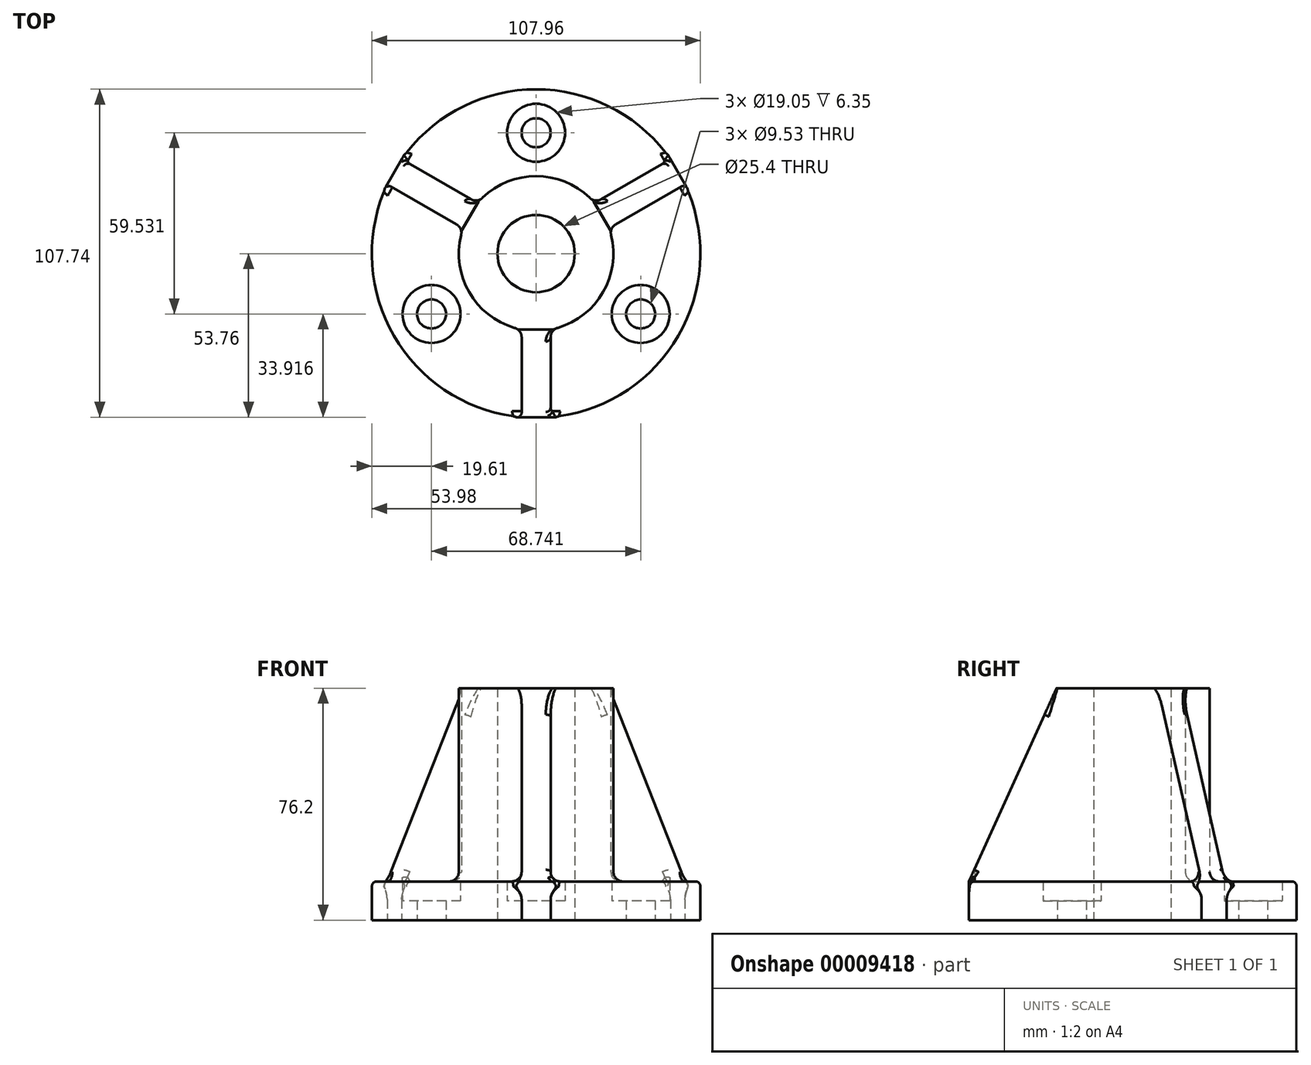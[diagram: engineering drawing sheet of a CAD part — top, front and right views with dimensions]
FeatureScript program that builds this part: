
annotation { "Feature Type Name" : "Feature", "Feature Type Description" : "" }
export const myFeature = defineFeature(function(context is Context, id is Id, definition is map)
    precondition{}
    {
        {
            var Q0;
            Q0=qCreatedBy(makeId("Top.planeOp"),FACE);
            var sketch = newSketch(context, id + "F0", { "sketchPlane" : qUnion([Q0])});
            skArc(sketch, "E0", {"start": v(-48.94, 22.76) * mm, "mid": v(-46.74, -26.99) * mm, "end": v(-4.76, -53.76) * mm});
            skArc(sketch, "E1", {"start": v(-23.99, 8.35) * mm, "mid": v(-22, -12.7) * mm, "end": v(-4.76, -24.95) * mm});
            skCircle(sketch, "E2", {"center": v(0, 0) * mm, "radius": 12.7 * mm});
            skCircle(sketch, "E3", {"center": v(0, 39.69) * mm, "radius": 4.76 * mm});
            skCircle(sketch, "E4", {"center": v(0, 39.69) * mm, "radius": 9.53 * mm});
            skCircle(sketch, "E5.1.0", {"center": v(-34.37, -19.84) * mm, "radius": 4.76 * mm});
            skCircle(sketch, "E5.1.1", {"center": v(-34.37, -19.84) * mm, "radius": 9.53 * mm});
            skCircle(sketch, "E5.2.0", {"center": v(34.37, -19.84) * mm, "radius": 4.76 * mm});
            skCircle(sketch, "E5.2.1", {"center": v(34.37, -19.84) * mm, "radius": 9.53 * mm});
            skLineSegment(sketch, "E6", {"start": v(0, 0) * mm, "end": v(-73.96, 42.7) * mm, "construction": true});
            skLineSegment(sketch, "E7", {"start": v(-23.99, 8.35) * mm, "end": v(-19.23, 16.6) * mm});
            skLineSegment(sketch, "E8", {"start": v(-19.23, 16.6) * mm, "end": v(-44.18, 31) * mm});
            skLineSegment(sketch, "E9", {"start": v(-23.99, 8.35) * mm, "end": v(-48.94, 22.76) * mm});
            skLineSegment(sketch, "E10.1.0", {"start": v(-4.76, -24.95) * mm, "end": v(-4.76, -53.76) * mm});
            skLineSegment(sketch, "E10.1.1", {"start": v(4.76, -24.95) * mm, "end": v(4.76, -53.76) * mm});
            skLineSegment(sketch, "E10.1.2", {"start": v(4.76, -24.95) * mm, "end": v(-4.76, -24.95) * mm});
            skLineSegment(sketch, "E10.2.0", {"start": v(23.99, 8.35) * mm, "end": v(48.94, 22.76) * mm});
            skLineSegment(sketch, "E10.2.1", {"start": v(19.23, 16.6) * mm, "end": v(44.18, 31) * mm});
            skLineSegment(sketch, "E10.2.2", {"start": v(19.23, 16.6) * mm, "end": v(23.99, 8.35) * mm});
            skArc(sketch, "E11.trimOffspring", {"start": v(19.23, 16.6) * mm, "mid": v(0, 25.4) * mm, "end": v(-19.23, 16.6) * mm});
            skArc(sketch, "E12.trimOffspring", {"start": v(4.76, -24.95) * mm, "mid": v(22, -12.7) * mm, "end": v(23.99, 8.35) * mm});
            skArc(sketch, "E13.trimOffspring", {"start": v(4.76, -53.76) * mm, "mid": v(46.74, -26.99) * mm, "end": v(48.94, 22.76) * mm});
            skArc(sketch, "E14.trimOffspring", {"start": v(44.18, 31) * mm, "mid": v(0, 53.98) * mm, "end": v(-44.18, 31) * mm});
            skLineSegment(sketch, "E15", {"start": v(-4.76, -53.76) * mm, "end": v(4.76, -53.76) * mm});
            skLineSegment(sketch, "E16", {"start": v(48.94, 22.76) * mm, "end": v(44.18, 31) * mm});
            skLineSegment(sketch, "E17", {"start": v(-48.94, 22.76) * mm, "end": v(-44.18, 31) * mm});
            skSolve(sketch);
        }
        {
            var Q0;
            Q0=makeQuery(id+"F0.imprint","IMPRINT",FACE,{"disambiguationData":[TD([[makeQuery(id+"F0.imprint","IMPRINT",EDGE,{"derivedFrom":sQuery(id+"F0.wireOp",EDGE,"E1")}),1.0]])]});
            var Q1;
            Q1=makeQuery(id+"F0.imprint","IMPRINT",FACE,{"disambiguationData":[TD([[makeQuery(id+"F0.imprint","IMPRINT",EDGE,{"derivedFrom":sQuery(id+"F0.wireOp",EDGE,"E7")}),1.0]])]});
            var Q2;
            {var subQ1=sQuery(id+"F0.wireOp",EDGE,"E10.2.0");Q2=makeQuery(id+"F0.imprint","IMPRINT",FACE,{"disambiguationData":[TD([[makeQuery(id+"F0.imprint","IMPRINT",EDGE,{"derivedFrom":subQ1}),1.0]])]});}
            var Q3;
            {var subQ1=sQuery(id+"F0.wireOp",EDGE,"E10.1.0");Q3=makeQuery(id+"F0.imprint","IMPRINT",FACE,{"disambiguationData":[TD([[makeQuery(id+"F0.imprint","IMPRINT",EDGE,{"derivedFrom":subQ1}),1.0]])]});}
            extrude(context, id + "F1", {"entities" : qUnion([Q0, Q1, Q2, Q3]), "depth" : 76.2 * mm});
        }
        {
            var Q0;
            Q0=makeQuery(id+"F0.imprint","IMPRINT",FACE,{"disambiguationData":[TD([[makeQuery(id+"F0.imprint","IMPRINT",EDGE,{"derivedFrom":sQuery(id+"F0.wireOp",EDGE,"E4")}),-1.0]])]});
            var Q1;
            {var subQ1=sQuery(id+"F0.wireOp",EDGE,"E10.2.0");Q1=makeQuery(id+"F0.imprint","IMPRINT",FACE,{"disambiguationData":[TD([[makeQuery(id+"F0.imprint","IMPRINT",EDGE,{"derivedFrom":subQ1}),1.0]])]});}
            var Q2;
            Q2=makeQuery(id+"F0.imprint","IMPRINT",FACE,{"disambiguationData":[TD([[makeQuery(id+"F0.imprint","IMPRINT",EDGE,{"derivedFrom":sQuery(id+"F0.wireOp",EDGE,"E5.2.1")}),-1.0]])]});
            var Q3;
            {var subQ1=sQuery(id+"F0.wireOp",EDGE,"E10.1.0");Q3=makeQuery(id+"F0.imprint","IMPRINT",FACE,{"disambiguationData":[TD([[makeQuery(id+"F0.imprint","IMPRINT",EDGE,{"derivedFrom":subQ1}),1.0]])]});}
            var Q4;
            Q4=makeQuery(id+"F0.imprint","IMPRINT",FACE,{"disambiguationData":[TD([[makeQuery(id+"F0.imprint","IMPRINT",EDGE,{"derivedFrom":sQuery(id+"F0.wireOp",EDGE,"E1")}),-1.0]])]});
            var Q5;
            Q5=makeQuery(id+"F0.imprint","IMPRINT",FACE,{"disambiguationData":[TD([[makeQuery(id+"F0.imprint","IMPRINT",EDGE,{"derivedFrom":sQuery(id+"F0.wireOp",EDGE,"E7")}),1.0]])]});
            extrude(context, id + "F2", {"entities" : qUnion([Q0, Q1, Q2, Q3, Q4, Q5]), "operationType" : NewBodyOperationType.ADD, "depth" : 12.7 * mm});
        }
        {
            var Q0;
            Q0=makeQuery(id+"F0.imprint","IMPRINT",FACE,{"disambiguationData":[TD([[makeQuery(id+"F0.imprint","IMPRINT",EDGE,{"derivedFrom":sQuery(id+"F0.wireOp",EDGE,"E5.1.0")}),-1.0]])]});
            var Q1;
            Q1=makeQuery(id+"F0.imprint","IMPRINT",FACE,{"disambiguationData":[TD([[makeQuery(id+"F0.imprint","IMPRINT",EDGE,{"derivedFrom":sQuery(id+"F0.wireOp",EDGE,"E3")}),-1.0]])]});
            var Q2;
            Q2=makeQuery(id+"F0.imprint","IMPRINT",FACE,{"disambiguationData":[TD([[makeQuery(id+"F0.imprint","IMPRINT",EDGE,{"derivedFrom":sQuery(id+"F0.wireOp",EDGE,"E5.2.0")}),-1.0]])]});
            extrude(context, id + "F3", {"entities" : qUnion([Q0, Q1, Q2]), "operationType" : NewBodyOperationType.ADD, "depth" : 6.35 * mm});
        }
        {
            var Q0;
            Q0=makeQuery(id+"F1.opExtrude","SWEPT_FACE",FACE,{"disambiguationData":[OSD([sQuery(id+"F0.wireOp",EDGE,"E9")])]});
            var sketch = newSketch(context, id + "F4", { "sketchPlane" : qUnion([Q0])});
            skLineSegment(sketch, "E18", {"start": v(-24.95, 12.7) * mm, "end": v(-53.76, 12.7) * mm});
            skLineSegment(sketch, "E19", {"start": v(-53.76, 12.7) * mm, "end": v(-24.95, 76.2) * mm});
            skLineSegment(sketch, "E20", {"start": v(-24.95, 76.2) * mm, "end": v(-24.95, 12.7) * mm});
            skSolve(sketch);
        }
        {
            var Q0;
            Q0=makeQuery(id+"F1.opExtrude","SWEPT_FACE",FACE,{"disambiguationData":[OSD([sQuery(id+"F0.wireOp",EDGE,"E10.1.0")])]});
            var sketch = newSketch(context, id + "F5", { "sketchPlane" : qUnion([Q0])});
            skLineSegment(sketch, "E21", {"start": v(53.76, 12.7) * mm, "end": v(24.95, 12.7) * mm});
            skLineSegment(sketch, "E22", {"start": v(24.95, 12.7) * mm, "end": v(24.95, 76.2) * mm});
            skLineSegment(sketch, "E23", {"start": v(24.95, 76.2) * mm, "end": v(53.76, 12.7) * mm});
            skSolve(sketch);
        }
        {
            var Q0;
            Q0=makeQuery(id+"F1.opExtrude","SWEPT_FACE",FACE,{"disambiguationData":[OSD([sQuery(id+"F0.wireOp",EDGE,"E10.2.0")])]});
            var sketch = newSketch(context, id + "F6", { "sketchPlane" : qUnion([Q0])});
            skLineSegment(sketch, "E24", {"start": v(24.95, 76.2) * mm, "end": v(53.76, 12.7) * mm});
            skLineSegment(sketch, "E25", {"start": v(53.76, 12.7) * mm, "end": v(24.95, 12.7) * mm});
            skLineSegment(sketch, "E26", {"start": v(24.95, 12.7) * mm, "end": v(24.95, 76.2) * mm});
            skSolve(sketch);
        }
        {
            var Q0;
            Q0=makeQuery(id+"F6.imprint","IMPRINT",FACE,{"disambiguationData":[TD([[makeQuery(id+"F6.imprint","IMPRINT",EDGE,{"derivedFrom":sQuery(id+"F6.wireOp",EDGE,"E24")}),1.0]])]});
            extrude(context, id + "F7", {"entities" : qUnion([Q0]), "operationType" : NewBodyOperationType.REMOVE, "oppositeDirection" : true, "depth" : 25.4 * mm});
        }
        {
            var Q0;
            Q0=makeQuery(id+"F5.imprint","IMPRINT",FACE,{"disambiguationData":[TD([[makeQuery(id+"F5.imprint","IMPRINT",EDGE,{"derivedFrom":sQuery(id+"F5.wireOp",EDGE,"E23")}),1.0]])]});
            extrude(context, id + "F8", {"entities" : qUnion([Q0]), "operationType" : NewBodyOperationType.REMOVE, "oppositeDirection" : true, "depth" : 25.4 * mm});
        }
        {
            var Q0;
            Q0=makeQuery(id+"F4.imprint","IMPRINT",FACE,{"disambiguationData":[TD([[makeQuery(id+"F4.imprint","IMPRINT",EDGE,{"derivedFrom":sQuery(id+"F4.wireOp",EDGE,"E19")}),1.0]])]});
            extrude(context, id + "F9", {"entities" : qUnion([Q0]), "operationType" : NewBodyOperationType.REMOVE, "oppositeDirection" : true, "depth" : 25.4 * mm});
        }
        {
            var Q0;
            Q0=makeQuery(id+"F2.opExtrude","CAP_EDGE",EDGE,{"disambiguationData":[OSD([sQuery(id+"F0.wireOp",EDGE,"E14.trimOffspring")])],"isStart":false});
            var Q1;
            Q1=makeQuery(id+"F2.opExtrude","CAP_EDGE",EDGE,{"disambiguationData":[OSD([sQuery(id+"F0.wireOp",EDGE,"E13.trimOffspring")])],"isStart":false});
            var Q2;
            Q2=makeQuery(id+"F2.opExtrude","CAP_EDGE",EDGE,{"disambiguationData":[OSD([sQuery(id+"F0.wireOp",EDGE,"E0")])],"isStart":false});
            fillet(context, id + "F10", {"entities" : qUnion([Q0, Q1, Q2]), "radius" : 1.59 * mm, "tangentPropagation" : true, "allowEdgeOverflow" : false});
        }
        {
            var Q0;
            Q0=makeQuery(id+"F1.opExtrude","SWEPT_EDGE",EDGE,{"disambiguationData":[OSD([sQuery(id+"F0.wireOp",EDGE,"E1"),sQuery(id+"F0.wireOp",EDGE,"E7"),sQuery(id+"F0.wireOp",EDGE,"E9")])]});
            var Q1;
            Q1=makeQuery(id+"F1.opExtrude","SWEPT_EDGE",EDGE,{"disambiguationData":[OSD([sQuery(id+"F0.wireOp",EDGE,"E1"),sQuery(id+"F0.wireOp",EDGE,"E10.1.0"),sQuery(id+"F0.wireOp",EDGE,"E10.1.2")])]});
            var Q2;
            Q2=makeQuery(id+"F1.opExtrude","SWEPT_EDGE",EDGE,{"disambiguationData":[OSD([sQuery(id+"F0.wireOp",EDGE,"E10.1.1"),sQuery(id+"F0.wireOp",EDGE,"E10.1.2"),sQuery(id+"F0.wireOp",EDGE,"E12.trimOffspring")])]});
            var Q3;
            Q3=makeQuery(id+"F1.opExtrude","SWEPT_EDGE",EDGE,{"disambiguationData":[OSD([sQuery(id+"F0.wireOp",EDGE,"E10.2.0"),sQuery(id+"F0.wireOp",EDGE,"E10.2.2"),sQuery(id+"F0.wireOp",EDGE,"E12.trimOffspring")])]});
            var Q4;
            Q4=makeQuery(id+"F1.opExtrude","SWEPT_EDGE",EDGE,{"disambiguationData":[OSD([sQuery(id+"F0.wireOp",EDGE,"E10.2.1"),sQuery(id+"F0.wireOp",EDGE,"E10.2.2"),sQuery(id+"F0.wireOp",EDGE,"E11.trimOffspring")])]});
            var Q5;
            Q5=makeQuery(id+"F1.opExtrude","SWEPT_EDGE",EDGE,{"disambiguationData":[OSD([sQuery(id+"F0.wireOp",EDGE,"E7"),sQuery(id+"F0.wireOp",EDGE,"E8"),sQuery(id+"F0.wireOp",EDGE,"E11.trimOffspring")])]});
            var Q6;
            Q6=makeQuery(id+"F2.opExtrude","CAP_EDGE",EDGE,{"disambiguationData":[OSD([sQuery(id+"F0.wireOp",EDGE,"E11.trimOffspring")])],"isStart":false});
            var Q7;
            Q7=makeQuery(id+"F2.opExtrude","CAP_EDGE",EDGE,{"disambiguationData":[OSD([sQuery(id+"F0.wireOp",EDGE,"E12.trimOffspring")])],"isStart":false});
            var Q8;
            Q8=makeQuery(id+"F2.opExtrude","CAP_EDGE",EDGE,{"disambiguationData":[OSD([sQuery(id+"F0.wireOp",EDGE,"E1")])],"isStart":false});
            fillet(context, id + "F11", {"entities" : qUnion([Q0, Q1, Q2, Q3, Q4, Q5, Q6, Q7, Q8]), "radius" : 3.17 * mm, "allowEdgeOverflow" : false});
        }
        {
            var Q0;
            Q0=makeQuery(id+"F2.boolean.opBoolean","INTERSECT",EDGE,{"derivedFrom":[makeQuery(id+"F1.opExtrude","SWEPT_FACE",FACE,{"disambiguationData":[OSD([sQuery(id+"F0.wireOp",EDGE,"E10.1.1")])]}),makeQuery(id+"F2.opExtrude","CAP_FACE",FACE,{"disambiguationData":[OSD([sQuery(id+"F0.wireOp",EDGE,"E0"),sQuery(id+"F0.wireOp",EDGE,"E1"),sQuery(id+"F0.wireOp",EDGE,"E4"),sQuery(id+"F0.wireOp",EDGE,"E5.1.1"),sQuery(id+"F0.wireOp",EDGE,"E5.2.1"),sQuery(id+"F0.wireOp",EDGE,"E7"),sQuery(id+"F0.wireOp",EDGE,"E10.1.2"),sQuery(id+"F0.wireOp",EDGE,"E10.2.2"),sQuery(id+"F0.wireOp",EDGE,"E11.trimOffspring"),sQuery(id+"F0.wireOp",EDGE,"E12.trimOffspring"),sQuery(id+"F0.wireOp",EDGE,"E13.trimOffspring"),sQuery(id+"F0.wireOp",EDGE,"E14.trimOffspring"),sQuery(id+"F0.wireOp",EDGE,"E15"),sQuery(id+"F0.wireOp",EDGE,"E16"),sQuery(id+"F0.wireOp",EDGE,"E17")])],"isStart":false})]});
            var Q1;
            Q1=makeQuery(id+"F2.boolean.opBoolean","INTERSECT",EDGE,{"derivedFrom":[makeQuery(id+"F1.opExtrude","SWEPT_FACE",FACE,{"disambiguationData":[OSD([sQuery(id+"F0.wireOp",EDGE,"E10.2.0")])]}),makeQuery(id+"F2.opExtrude","CAP_FACE",FACE,{"disambiguationData":[OSD([sQuery(id+"F0.wireOp",EDGE,"E0"),sQuery(id+"F0.wireOp",EDGE,"E1"),sQuery(id+"F0.wireOp",EDGE,"E4"),sQuery(id+"F0.wireOp",EDGE,"E5.1.1"),sQuery(id+"F0.wireOp",EDGE,"E5.2.1"),sQuery(id+"F0.wireOp",EDGE,"E7"),sQuery(id+"F0.wireOp",EDGE,"E10.1.2"),sQuery(id+"F0.wireOp",EDGE,"E10.2.2"),sQuery(id+"F0.wireOp",EDGE,"E11.trimOffspring"),sQuery(id+"F0.wireOp",EDGE,"E12.trimOffspring"),sQuery(id+"F0.wireOp",EDGE,"E13.trimOffspring"),sQuery(id+"F0.wireOp",EDGE,"E14.trimOffspring"),sQuery(id+"F0.wireOp",EDGE,"E15"),sQuery(id+"F0.wireOp",EDGE,"E16"),sQuery(id+"F0.wireOp",EDGE,"E17")])],"isStart":false})]});
            var Q2;
            Q2=makeQuery(id+"F2.boolean.opBoolean","INTERSECT",EDGE,{"derivedFrom":[makeQuery(id+"F1.opExtrude","SWEPT_FACE",FACE,{"disambiguationData":[OSD([sQuery(id+"F0.wireOp",EDGE,"E10.2.1")])]}),makeQuery(id+"F2.opExtrude","CAP_FACE",FACE,{"disambiguationData":[OSD([sQuery(id+"F0.wireOp",EDGE,"E0"),sQuery(id+"F0.wireOp",EDGE,"E1"),sQuery(id+"F0.wireOp",EDGE,"E4"),sQuery(id+"F0.wireOp",EDGE,"E5.1.1"),sQuery(id+"F0.wireOp",EDGE,"E5.2.1"),sQuery(id+"F0.wireOp",EDGE,"E7"),sQuery(id+"F0.wireOp",EDGE,"E10.1.2"),sQuery(id+"F0.wireOp",EDGE,"E10.2.2"),sQuery(id+"F0.wireOp",EDGE,"E11.trimOffspring"),sQuery(id+"F0.wireOp",EDGE,"E12.trimOffspring"),sQuery(id+"F0.wireOp",EDGE,"E13.trimOffspring"),sQuery(id+"F0.wireOp",EDGE,"E14.trimOffspring"),sQuery(id+"F0.wireOp",EDGE,"E15"),sQuery(id+"F0.wireOp",EDGE,"E16"),sQuery(id+"F0.wireOp",EDGE,"E17")])],"isStart":false})]});
            var Q3;
            Q3=makeQuery(id+"F2.boolean.opBoolean","INTERSECT",EDGE,{"derivedFrom":[makeQuery(id+"F1.opExtrude","SWEPT_FACE",FACE,{"disambiguationData":[OSD([sQuery(id+"F0.wireOp",EDGE,"E8")])]}),makeQuery(id+"F2.opExtrude","CAP_FACE",FACE,{"disambiguationData":[OSD([sQuery(id+"F0.wireOp",EDGE,"E0"),sQuery(id+"F0.wireOp",EDGE,"E1"),sQuery(id+"F0.wireOp",EDGE,"E4"),sQuery(id+"F0.wireOp",EDGE,"E5.1.1"),sQuery(id+"F0.wireOp",EDGE,"E5.2.1"),sQuery(id+"F0.wireOp",EDGE,"E7"),sQuery(id+"F0.wireOp",EDGE,"E10.1.2"),sQuery(id+"F0.wireOp",EDGE,"E10.2.2"),sQuery(id+"F0.wireOp",EDGE,"E11.trimOffspring"),sQuery(id+"F0.wireOp",EDGE,"E12.trimOffspring"),sQuery(id+"F0.wireOp",EDGE,"E13.trimOffspring"),sQuery(id+"F0.wireOp",EDGE,"E14.trimOffspring"),sQuery(id+"F0.wireOp",EDGE,"E15"),sQuery(id+"F0.wireOp",EDGE,"E16"),sQuery(id+"F0.wireOp",EDGE,"E17")])],"isStart":false})]});
            var Q4;
            Q4=makeQuery(id+"F2.boolean.opBoolean","INTERSECT",EDGE,{"derivedFrom":[makeQuery(id+"F1.opExtrude","SWEPT_FACE",FACE,{"disambiguationData":[OSD([sQuery(id+"F0.wireOp",EDGE,"E9")])]}),makeQuery(id+"F2.opExtrude","CAP_FACE",FACE,{"disambiguationData":[OSD([sQuery(id+"F0.wireOp",EDGE,"E0"),sQuery(id+"F0.wireOp",EDGE,"E1"),sQuery(id+"F0.wireOp",EDGE,"E4"),sQuery(id+"F0.wireOp",EDGE,"E5.1.1"),sQuery(id+"F0.wireOp",EDGE,"E5.2.1"),sQuery(id+"F0.wireOp",EDGE,"E7"),sQuery(id+"F0.wireOp",EDGE,"E10.1.2"),sQuery(id+"F0.wireOp",EDGE,"E10.2.2"),sQuery(id+"F0.wireOp",EDGE,"E11.trimOffspring"),sQuery(id+"F0.wireOp",EDGE,"E12.trimOffspring"),sQuery(id+"F0.wireOp",EDGE,"E13.trimOffspring"),sQuery(id+"F0.wireOp",EDGE,"E14.trimOffspring"),sQuery(id+"F0.wireOp",EDGE,"E15"),sQuery(id+"F0.wireOp",EDGE,"E16"),sQuery(id+"F0.wireOp",EDGE,"E17")])],"isStart":false})]});
            var Q5;
            Q5=makeQuery(id+"F2.boolean.opBoolean","INTERSECT",EDGE,{"derivedFrom":[makeQuery(id+"F1.opExtrude","SWEPT_FACE",FACE,{"disambiguationData":[OSD([sQuery(id+"F0.wireOp",EDGE,"E10.1.0")])]}),makeQuery(id+"F2.opExtrude","CAP_FACE",FACE,{"disambiguationData":[OSD([sQuery(id+"F0.wireOp",EDGE,"E0"),sQuery(id+"F0.wireOp",EDGE,"E1"),sQuery(id+"F0.wireOp",EDGE,"E4"),sQuery(id+"F0.wireOp",EDGE,"E5.1.1"),sQuery(id+"F0.wireOp",EDGE,"E5.2.1"),sQuery(id+"F0.wireOp",EDGE,"E7"),sQuery(id+"F0.wireOp",EDGE,"E10.1.2"),sQuery(id+"F0.wireOp",EDGE,"E10.2.2"),sQuery(id+"F0.wireOp",EDGE,"E11.trimOffspring"),sQuery(id+"F0.wireOp",EDGE,"E12.trimOffspring"),sQuery(id+"F0.wireOp",EDGE,"E13.trimOffspring"),sQuery(id+"F0.wireOp",EDGE,"E14.trimOffspring"),sQuery(id+"F0.wireOp",EDGE,"E15"),sQuery(id+"F0.wireOp",EDGE,"E16"),sQuery(id+"F0.wireOp",EDGE,"E17")])],"isStart":false})]});
            fillet(context, id + "F12", {"entities" : qUnion([Q0, Q1, Q2, Q3, Q4, Q5]), "radius" : 3.17 * mm, "tangentPropagation" : true, "allowEdgeOverflow" : false});
        }
        {
            var Q0;
            Q0=makeQuery(id+"F7.boolean.opBoolean","COPY",EDGE,{"derivedFrom":makeQuery(id+"F7.opExtrude","CAP_EDGE",EDGE,{"disambiguationData":[OSD([sQuery(id+"F6.wireOp",EDGE,"E24")])],"isStart":true})});
            var Q1;
            Q1=makeQuery(id+"F7.boolean.opBoolean","INTERSECT",EDGE,{"derivedFrom":[makeQuery(id+"F1.opExtrude","SWEPT_FACE",FACE,{"disambiguationData":[OSD([sQuery(id+"F0.wireOp",EDGE,"E10.2.1")])]}),makeQuery(id+"F7.opExtrude","SWEPT_FACE",FACE,{"disambiguationData":[OSD([sQuery(id+"F6.wireOp",EDGE,"E24")])]})]});
            var Q2;
            Q2=makeQuery(id+"F8.boolean.opBoolean","COPY",EDGE,{"derivedFrom":makeQuery(id+"F8.opExtrude","CAP_EDGE",EDGE,{"disambiguationData":[OSD([sQuery(id+"F5.wireOp",EDGE,"E23")])],"isStart":true})});
            var Q3;
            Q3=makeQuery(id+"F8.boolean.opBoolean","INTERSECT",EDGE,{"derivedFrom":[makeQuery(id+"F1.opExtrude","SWEPT_FACE",FACE,{"disambiguationData":[OSD([sQuery(id+"F0.wireOp",EDGE,"E10.1.1")])]}),makeQuery(id+"F8.opExtrude","SWEPT_FACE",FACE,{"disambiguationData":[OSD([sQuery(id+"F5.wireOp",EDGE,"E23")])]})]});
            var Q4;
            Q4=makeQuery(id+"F9.boolean.opBoolean","INTERSECT",EDGE,{"derivedFrom":[makeQuery(id+"F1.opExtrude","SWEPT_FACE",FACE,{"disambiguationData":[OSD([sQuery(id+"F0.wireOp",EDGE,"E8")])]}),makeQuery(id+"F9.opExtrude","SWEPT_FACE",FACE,{"disambiguationData":[OSD([sQuery(id+"F4.wireOp",EDGE,"E19")])]})]});
            var Q5;
            Q5=makeQuery(id+"F9.boolean.opBoolean","COPY",EDGE,{"derivedFrom":makeQuery(id+"F9.opExtrude","CAP_EDGE",EDGE,{"disambiguationData":[OSD([sQuery(id+"F4.wireOp",EDGE,"E19")])],"isStart":true})});
            fillet(context, id + "F13", {"entities" : qUnion([Q0, Q1, Q2, Q3, Q4, Q5]), "radius" : 1.59 * mm, "tangentPropagation" : true, "allowEdgeOverflow" : false});
        }
    });
